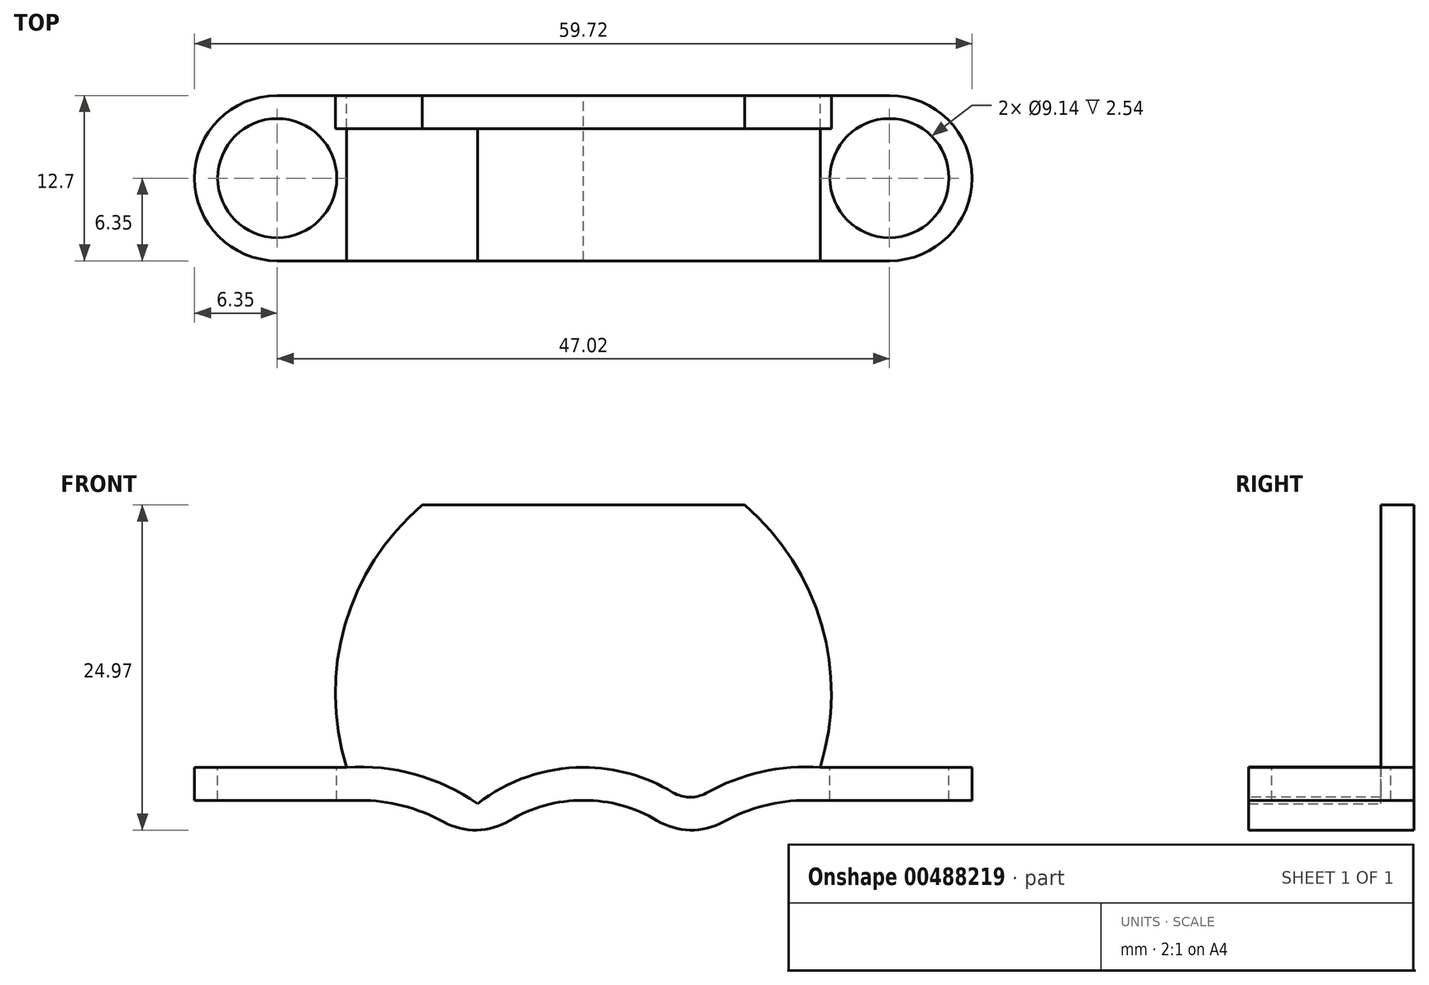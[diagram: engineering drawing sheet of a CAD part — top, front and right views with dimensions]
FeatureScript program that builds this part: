
annotation { "Feature Type Name" : "Feature", "Feature Type Description" : "" }
export const myFeature = defineFeature(function(context is Context, id is Id, definition is map)
    precondition{}
    {
        {
            var Q0;
            Q0=qCreatedBy(makeId("Front.planeOp"),FACE);
            var sketch = newSketch(context, id + "F0", { "sketchPlane" : qUnion([Q0])});
            skArc(sketch, "E0", {"start": v(-12.38, 14.48) * mm, "mid": v(-17.55, 7.41) * mm, "end": v(-19.01, -1.22) * mm});
            skLineSegment(sketch, "E1", {"start": v(-12.38, 14.48) * mm, "end": v(12.38, 14.48) * mm});
            skArc(sketch, "E2.trimOffspring", {"start": v(19.01, -1.22) * mm, "mid": v(17.55, 7.41) * mm, "end": v(12.38, 14.48) * mm});
            skLineSegment(sketch, "E3", {"start": v(-17.2, -8.2) * mm, "end": v(-29.86, -8.2) * mm});
            skLineSegment(sketch, "E4", {"start": v(17.2, -8.2) * mm, "end": v(29.86, -8.2) * mm});
            skLineSegment(sketch, "E5", {"start": v(-29.86, -8.2) * mm, "end": v(-29.86, -5.66) * mm});
            skLineSegment(sketch, "E6", {"start": v(29.86, -8.2) * mm, "end": v(29.86, -5.66) * mm});
            skLineSegment(sketch, "E7", {"start": v(29.86, -5.66) * mm, "end": v(18.19, -5.66) * mm});
            skLineSegment(sketch, "E8", {"start": v(-29.86, -5.66) * mm, "end": v(-18.19, -5.66) * mm});
            skArc(sketch, "E9", {"start": v(8.03, -11.83) * mm, "mid": v(-0.02, -8.2) * mm, "end": v(-8.1, -11.77) * mm});
            skArc(sketch, "E10", {"start": v(17.2, -8.2) * mm, "mid": v(12.27, -9.14) * mm, "end": v(8.03, -11.83) * mm});
            skArc(sketch, "E11", {"start": v(18.19, -5.66) * mm, "mid": v(12.92, -6.21) * mm, "end": v(8.13, -8.46) * mm});
            skArc(sketch, "E12.trimOffspring", {"start": v(-8.1, -11.77) * mm, "mid": v(-12.3, -9.13) * mm, "end": v(-17.2, -8.2) * mm});
            skArc(sketch, "E13.trimOffspring", {"start": v(18.19, -5.66) * mm, "mid": v(18.3, 5.28) * mm, "end": v(12.38, 14.48) * mm});
            skArc(sketch, "E14.trimOffspring", {"start": v(-8.19, -8.41) * mm, "mid": v(-12.96, -6.2) * mm, "end": v(-18.19, -5.66) * mm});
            skArc(sketch, "E15.trimOffspring", {"start": v(8.13, -8.46) * mm, "mid": v(-0.02, -5.66) * mm, "end": v(-8.19, -8.41) * mm});
            skArc(sketch, "E16.trimOffspring", {"start": v(-12.38, 14.48) * mm, "mid": v(-18.3, 5.28) * mm, "end": v(-18.19, -5.66) * mm});
            skSolve(sketch);
        }
        {
            var Q0;
            {var subQ2=sQuery(id+"F0.wireOp",EDGE,"E1");Q0=makeQuery(id+"F0.imprint","IMPRINT",FACE,{"disambiguationData":[TD([[makeQuery(id+"F0.imprint","IMPRINT",EDGE,{"derivedFrom":subQ2}),-1.0]])]});}
            extrude(context, id + "F1", {"entities" : qUnion([Q0]), "depth" : 2.54 * mm, "offsetDistance" : 25.4 * mm});
        }
        {
            var Q0;
            Q0=makeQuery(id+"F0.imprint","IMPRINT",FACE,{"disambiguationData":[TD([[makeQuery(id+"F0.imprint","IMPRINT",EDGE,{"derivedFrom":sQuery(id+"F0.wireOp",EDGE,"E3")}),-1.0]])]});
            extrude(context, id + "F2", {"entities" : qUnion([Q0]), "operationType" : NewBodyOperationType.ADD, "depth" : 12.7 * mm, "offsetDistance" : 25.4 * mm});
        }
        {
            var Q0;
            Q0=makeQuery(id+"F2.opExtrude","SWEPT_EDGE",EDGE,{"disambiguationData":[OSD([sQuery(id+"F0.wireOp",EDGE,"E9"),sQuery(id+"F0.wireOp",EDGE,"E12.trimOffspring")])]});
            var Q1;
            Q1=makeQuery(id+"F2.opExtrude","SWEPT_EDGE",EDGE,{"disambiguationData":[OSD([sQuery(id+"F0.wireOp",EDGE,"E9"),sQuery(id+"F0.wireOp",EDGE,"E10")])]});
            fillet(context, id + "F3", {"entities" : qUnion([Q0, Q1]), "radius" : 5.08 * mm, "tangentPropagation" : true, "allowEdgeOverflow" : false});
        }
        {
            var Q0;
            Q0=makeQuery(id+"F2.opExtrude","SWEPT_FACE",FACE,{"disambiguationData":[OSD([sQuery(id+"F0.wireOp",EDGE,"E8")])]});
            var sketch = newSketch(context, id + "F4", { "sketchPlane" : qUnion([Q0])});
            skLineSegment(sketch, "E17", {"start": v(-29.86, -6.35) * mm, "end": v(-23.51, -6.35) * mm});
            skCircle(sketch, "E18", {"center": v(-23.51, -6.35) * mm, "radius": 6.35 * mm});
            skCircle(sketch, "E19", {"center": v(-23.51, -6.35) * mm, "radius": 4.57 * mm});
            skSolve(sketch);
        }
        {
            var Q0;
            Q0=makeQuery(id+"F4.imprint","IMPRINT",FACE,{"disambiguationData":[TD([[makeQuery(id+"F4.imprint","IMPRINT",EDGE,{"derivedFrom":sQuery(id+"F4.wireOp",EDGE,"E19")}),1.0]])]});
            var Q1;
            {var subQ0=sQuery(id+"F4.wireOp",EDGE,"E18");var subQ1=sQuery(id+"F0.wireOp",EDGE,"E8");var subQ4=makeQuery(id+"F2.opExtrude","CAP_EDGE",EDGE,{"disambiguationData":[OSD([subQ1])],"isStart":true});var subQ5=makeQuery(id+"F4.imprint","INTERSECT",VERTEX,{"derivedFrom":[subQ4,subQ0]});Q1=makeQuery(id+"F4.imprint","IMPRINT",FACE,{"disambiguationData":[TD([[makeQuery(id+"F4.imprint","IMPRINT",EDGE,{"disambiguationData":[TD([[subQ5,-1.0]])],"derivedFrom":subQ0}),-1.0]])]});}
            var Q2;
            {var subQ0=sQuery(id+"F4.wireOp",EDGE,"E18");var subQ1=sQuery(id+"F0.wireOp",EDGE,"E8");var subQ4=makeQuery(id+"F2.opExtrude","CAP_EDGE",EDGE,{"disambiguationData":[OSD([subQ1])],"isStart":false});var subQ5=makeQuery(id+"F4.imprint","INTERSECT",VERTEX,{"derivedFrom":[subQ4,subQ0]});Q2=makeQuery(id+"F4.imprint","IMPRINT",FACE,{"disambiguationData":[TD([[makeQuery(id+"F4.imprint","IMPRINT",EDGE,{"disambiguationData":[TD([[subQ5,1.0]])],"derivedFrom":subQ0}),-1.0]])]});}
            extrude(context, id + "F5", {"entities" : qUnion([Q0, Q1, Q2]), "operationType" : NewBodyOperationType.REMOVE, "oppositeDirection" : true, "depth" : 25.4 * mm, "offsetDistance" : 25.4 * mm});
        }
        {
            var Q0;
            Q0=makeQuery(id+"F1.opExtrude","SWEPT_BODY",BODY,{"disambiguationData":[OSD([sQuery(id+"F0.wireOp",EDGE,"E1"),sQuery(id+"F0.wireOp",EDGE,"E11"),sQuery(id+"F0.wireOp",EDGE,"E13.trimOffspring"),sQuery(id+"F0.wireOp",EDGE,"E14.trimOffspring"),sQuery(id+"F0.wireOp",EDGE,"E15.trimOffspring"),sQuery(id+"F0.wireOp",EDGE,"E16.trimOffspring")])]});
            var Q1;
            Q1=qCreatedBy(makeId("Right.planeOp"),FACE);
            mirror(context, id + "F6", {"operationType" : NewBodyOperationType.INTERSECT, "entities" : qUnion([Q0]), "mirrorPlane" : qUnion([Q1])});
        }
        {
            var Q0;
            Q0=makeQuery(id+"F6.boolean.opBoolean","COPY",EDGE,{"derivedFrom":makeQuery(id+"F6.boolean.toolComplement.opBoolean","COPY",EDGE,{"derivedFrom":makeQuery(id+"F6.opPattern","COPY",EDGE,{"derivedFrom":makeQuery(id+"F2.opExtrude","SWEPT_EDGE",EDGE,{"disambiguationData":[OSD([sQuery(id+"F0.wireOp",EDGE,"E11"),sQuery(id+"F0.wireOp",EDGE,"E15.trimOffspring")])]}),"instanceName":"1"})})});
            var Q1;
            Q1=makeQuery(id+"F2.opExtrude","SWEPT_EDGE",EDGE,{"disambiguationData":[OSD([sQuery(id+"F0.wireOp",EDGE,"E11"),sQuery(id+"F0.wireOp",EDGE,"E15.trimOffspring")])]});
            fillet(context, id + "F7", {"entities" : qUnion([Q0, Q1]), "radius" : 2.54 * mm, "tangentPropagation" : true, "allowEdgeOverflow" : false});
        }
    });
